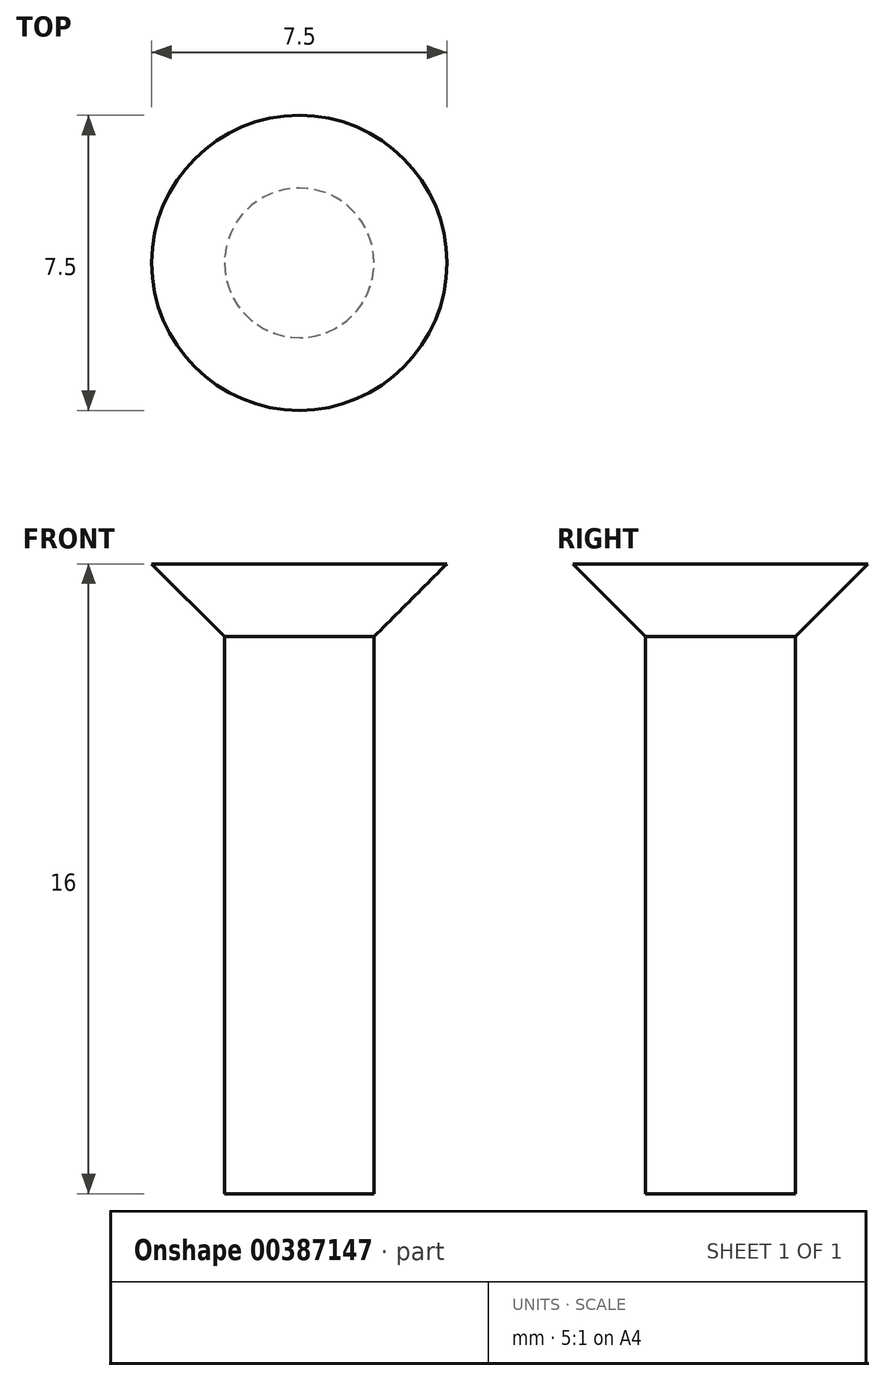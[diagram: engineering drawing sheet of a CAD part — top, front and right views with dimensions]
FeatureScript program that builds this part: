
annotation { "Feature Type Name" : "Feature", "Feature Type Description" : "" }
export const myFeature = defineFeature(function(context is Context, id is Id, definition is map)
    precondition{}
    {
        {
            var Q0;
            Q0=qCreatedBy(makeId("Top.planeOp"),FACE);
            var sketch = newSketch(context, id + "F0", { "sketchPlane" : qUnion([Q0])});
            skCircle(sketch, "E0", {"center": v(0, 0) * mm, "radius": 3.75 * mm});
            skSolve(sketch);
        }
        {
            var Q0;
            Q0 = qSketchRegion(id + "F0", true);
            extrude(context, id + "F1", {"entities" : qUnion([Q0]), "depth" : 2 * mm});
        }
        {
            var Q0;
            Q0=makeQuery(id+"F1.opExtrude","CAP_FACE",FACE,{"disambiguationData":[OSD([sQuery(id+"F0.wireOp",EDGE,"E0")])],"isStart":true});
            var sketch = newSketch(context, id + "F2", { "sketchPlane" : qUnion([Q0])});
            skCircle(sketch, "E1", {"center": v(0, 0) * mm, "radius": 1.9 * mm});
            skSolve(sketch);
        }
        {
            var Q0;
            Q0 = qSketchRegion(id + "F2", true);
            extrude(context, id + "F3", {"entities" : qUnion([Q0]), "operationType" : NewBodyOperationType.ADD, "depth" : 14 * mm});
        }
        {
            var Q0;
            Q0=makeQuery(id+"F1.opExtrude","CAP_EDGE",EDGE,{"disambiguationData":[OSD([sQuery(id+"F0.wireOp",EDGE,"E0")])],"isStart":true});
            chamfer(context, id + "F4", {"entities" : qUnion([Q0]), "width" : 2 * mm, "tangentPropagation" : true});
        }
    });
